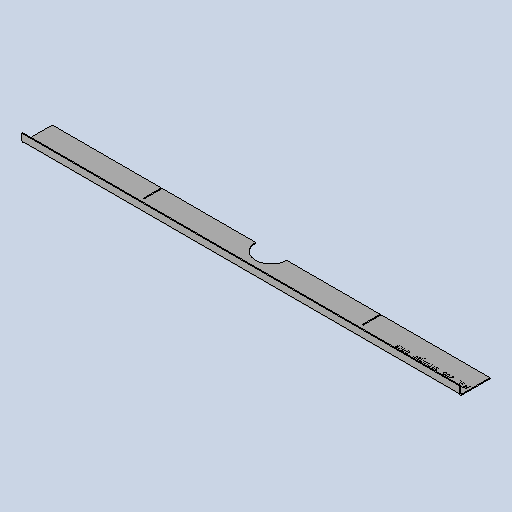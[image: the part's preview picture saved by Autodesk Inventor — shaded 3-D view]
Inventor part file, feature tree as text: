
AUTODESK INVENTOR PART (.ipt)
format: ipt  version: 2025 (Build 290162010, 162A)  size: 285,696 bytes
history: native  units: mm
features: other x5, sheet_metal_op x4, sketch x4, extrude x1
ambient origin geometry x8: Origin, YZ Plane, XZ Plane, XY Plane, X Axis, Y Axis, Z Axis, Center Point
bodies: Solid1 (feature_tree)
feature tree (14):
  sheet_metal_op  "Face1"
  sheet_metal_op  "Flange1"
  extrude  "Extrusion1"  Depth=68.0mm
  other  "Mark2"
  other  "A-Side Definition"
  sketch  "Sketch1"  dims[d0=980.0mm d1=68.0mm]
  other  "Plate1"
  sketch  "Sketch2"  dims[d2=2.0mm]
  other  "Plate2"
  sheet_metal_op  "Bend1"
  sheet_metal_op  "Corner1"
  sketch  "Sketch5"  dims[d3=2.0mm]
  sketch  "Sketch9"  dims[d4=1.0mm d5=4.0mm d6=2.75mm d7=20.0mm d8=90.0deg d9=2.75mm d10=8.0mm d11=2.0mm d12=2.75mm d15=0.0mm d16=0.0mm d40=200.0mm d41=12.0mm d45=70.0mm d48=2.1mm d49=490.0mm d51=29.0mm d52=39.0mm]
  other  "Definition1"
